# Revit family: Pressalit CT 4000 – Height adjustable
name_source: partatom
category: Specialty Equipment
units: mm (PartAtom-declared; Revit-internal decimal feet)

## family parameters
Always vertical = Yes
Cut with Voids When Loaded = No
Part Type = Normal
Room Calculation Point = No
Round Connector Dimension = Use Diameter
Shared = No
Work Plane-Based = No

## types (1)
- R8584572 - Long, adjustable height, manually foldable
    AdjustmentHeight = 700
    ColourOptions = 000 White
    Default Elevation = 0 mm  [stored 0 ft]
    Description = CT 4000 change table, manually foldable, electrically height adjustable, 1829 mm
    Electric = Yes
    Features = Manually foldable. Electrically height adjustable 700 mm; from 300 mm -1000 mm, with buttons placed in table front. Incl. safety rail, body belt and wired remote control.
    Fixed = No
    IntegralAccessories = Wired hand control, safety rail and body belt.
    Manufacturer = Pressalit A/S
    ManufacturerName = Pressalit A/S
    ManufacturerURL = https://pressalit.com
    Material = Powder-laquered stainless steel, lying surface in compact laminate.
    Material White = Pressalit - 000 White
    MaximumLoad = 200 kg
    Model = R8584572
    ModelNumber = R8584572
    ModelReference = R8584572
    NBSDescription = CT 4000 change table, manually foldable, electrically height adjustable, 1829 mm
    Name = CT 4000
    NominalHeight = 1180 mm  [stored 3.87139 ft]
    NominalLength = 1829 mm  [stored 6.00066 ft]
    NominalWidth = 1008 mm  [stored 3.30709 ft]
    Pressalit Product Number = R8584572xxx
    Pressalit Product Series = CT 4000
    ProductInformation = CT 4000 change table, manually foldable. Electrically height adjustable 700 mm; from 300 mm -1000 mm, with buttons placed in table front. Incl. safety rail, body belt and wired remote control. Lying surface 813 x 1829 mm in compact laminate. Outer measurements 1008 mm x 1829 mm. Excl. mounting kit.
    Size = 1829 x 1008 x 1180 mm
    URL = https://pressalit.com
    Version = 2022-12-03
    WarrantyDescription = Pressalit makes a commitment to remedy material and manufacturing defects for a period of three years from the invoicing date.
    WarrantyDurationLabor = To be filled out by contractor.
    WarrantyDurationParts = 3
    WarrantyDurationUnit = Years
    WarrantyGuarantorLabor = To be filled out by contractor.
    WarrantyStartDate = Invoicing date.
    Weight = 80 kg

note: [stored X ft] marks values corroborated as IEEE doubles in the binary element streams (Revit-internal decimal feet)

## geometry (parser evidence)
native form markers: Sweep x15
no freeform markers — native parametric forms only
